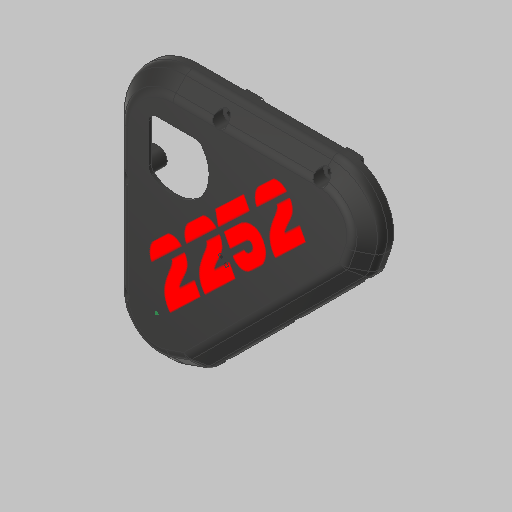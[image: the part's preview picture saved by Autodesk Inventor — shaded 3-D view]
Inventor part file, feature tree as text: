
AUTODESK INVENTOR PART (.ipt)
format: ipt  version: 2023.5 (Build 275446000, 446)  size: 399,872 bytes
history: native  units: in
note: dims shown in document units (in); Inventor stores cm internally (conversion verified against a paired STEP export)
features: fillet x2, extrude x1, sketch x1
ambient origin geometry x8: Origin, YZ Plane, XZ Plane, XY Plane, X Axis, Y Axis, Z Axis, Center Point
bodies: Solid2 (feature_tree), Solid1 (feature_tree)
feature tree (4):
  extrude  "Extrusion1"  Depth=0.25in
  fillet  "Fillet1"  Radius=1.0in
  fillet  "Fillet2"  Radius=0.05in
  sketch  "Sketch2"  dims[d0=0.25in d1=0.25in d2=1.0in d3=0.0in d4=0.05in d5=0.025in]
